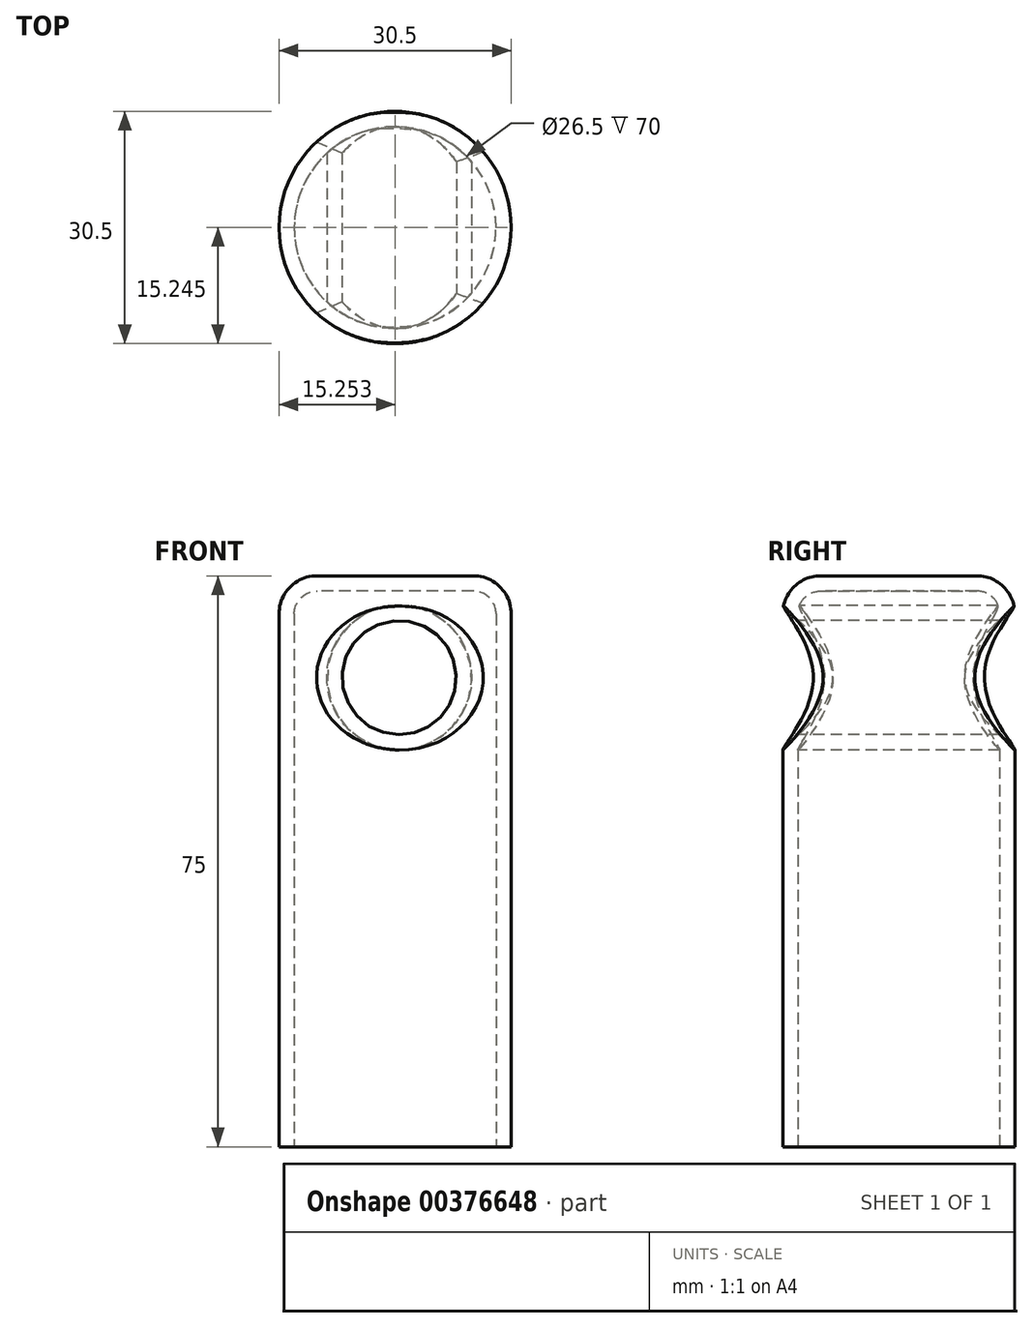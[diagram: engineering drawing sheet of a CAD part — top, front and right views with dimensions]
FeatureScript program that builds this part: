
annotation { "Feature Type Name" : "Feature", "Feature Type Description" : "" }
export const myFeature = defineFeature(function(context is Context, id is Id, definition is map)
    precondition{}
    {
        {
            var Q0;
            Q0=qCreatedBy(makeId("Top.planeOp"),FACE);
            var sketch = newSketch(context, id + "F0", { "sketchPlane" : qUnion([Q0])});
            skCircle(sketch, "E0", {"center": v(11.26, 11.54) * mm, "radius": 13.25 * mm});
            skCircle(sketch, "E1", {"center": v(11.26, 11.54) * mm, "radius": 15.25 * mm});
            skSolve(sketch);
        }
        {
            var Q0;
            Q0 = qSketchRegion(id + "F0", true);
            extrude(context, id + "F1", {"entities" : qUnion([Q0]), "depth" : 50 * mm});
        }
        {
            var Q0;
            Q0=makeQuery(id+"F1.opExtrude","CAP_FACE",FACE,{"disambiguationData":[OSD([sQuery(id+"F0.wireOp",EDGE,"E0"),sQuery(id+"F0.wireOp",EDGE,"E1")])],"isStart":false});
            var sketch = newSketch(context, id + "F2", { "sketchPlane" : qUnion([Q0])});
            skCircle(sketch, "E2", {"center": v(11.26, 11.54) * mm, "radius": 15.25 * mm});
            skSolve(sketch);
        }
        {
            var Q0;
            Q0 = qSketchRegion(id + "F2", true);
            extrude(context, id + "F3", {"entities" : qUnion([Q0]), "operationType" : NewBodyOperationType.ADD, "depth" : 25 * mm});
        }
        {
            var Q0;
            Q0=makeQuery(id+"F3.opExtrude","CAP_EDGE",EDGE,{"disambiguationData":[OSD([sQuery(id+"F2.wireOp",EDGE,"E2")])],"isStart":false});
            chamfer(context, id + "F4", {"entities" : qUnion([Q0]), "chamferType" : ChamferType.OFFSET_ANGLE, "width" : 14 * mm, "oppositeDirection" : false, "angle" : 60 * degree, "tangentPropagation" : true});
        }
        {
            var Q0;
            Q0=makeQuery(id+"F3.opExtrude","CAP_FACE",FACE,{"disambiguationData":[OSD([sQuery(id+"F2.wireOp",EDGE,"E2")])],"isStart":true});
            shell(context, id + "F5", {"entities" : qUnion([Q0]), "thickness" : 2 * mm});
        }
        {
            var Q0;
            Q0=makeQuery(id+"F3.opExtrude","CAP_FACE",FACE,{"disambiguationData":[OSD([sQuery(id+"F2.wireOp",EDGE,"E2")])],"isStart":false});
            var sketch = newSketch(context, id + "F6", { "sketchPlane" : qUnion([Q0])});
            skCircle(sketch, "E3", {"center": v(11.26, 11.54) * mm, "radius": 15.25 * mm});
            skSolve(sketch);
        }
        {
            var Q0;
            Q0 = qSketchRegion(id + "F6", true);
            extrude(context, id + "F7", {"entities" : qUnion([Q0]), "operationType" : NewBodyOperationType.ADD, "oppositeDirection" : true, "depth" : 25 * mm});
        }
        {
            var Q0;
            Q0=qCreatedBy(makeId("Front.planeOp"),FACE);
            var sketch = newSketch(context, id + "F8", { "sketchPlane" : qUnion([Q0])});
            skCircle(sketch, "E4", {"center": v(11.8, 61.62) * mm, "radius": 7.5 * mm});
            skSolve(sketch);
        }
        {
            var Q0;
            Q0 = qSketchRegion(id + "F8", true);
            extrude(context, id + "F9", {"entities" : qUnion([Q0]), "operationType" : NewBodyOperationType.REMOVE, "endBound" : BoundingType.THROUGH_ALL, "oppositeDirection" : true, "depth" : 25 * mm, "hasSecondDirection" : true, "secondDirectionBound" : SecondDirectionBoundingType.THROUGH_ALL, "secondDirectionOppositeDirection" : false, "secondDirectionDepth" : 25 * mm});
        }
        {
            var Q0;
            Q0=makeQuery(id+"F7.opExtrude","CAP_EDGE",EDGE,{"disambiguationData":[OSD([sQuery(id+"F6.wireOp",EDGE,"E3")])],"isStart":true});
            fillet(context, id + "F10", {"entities" : qUnion([Q0]), "radius" : 5 * mm, "tangentPropagation" : true, "allowEdgeOverflow" : false});
        }
        {
            var Q0;
            Q0=makeQuery(id+"F7.opExtrude","CAP_FACE",FACE,{"disambiguationData":[OSD([sQuery(id+"F6.wireOp",EDGE,"E3")])],"isStart":false});
            shell(context, id + "F11", {"entities" : qUnion([Q0]), "thickness" : 2 * mm});
        }
        {
            var Q0;
            Q0=makeQuery(id+"F9.boolean.opBoolean","INTERSECT",EDGE,{"disambiguationData":[OD(1.0)],"derivedFrom":[makeQuery(id+"F7.boolean.opBoolean","MERGE",FACE,{"derivedFrom":[makeQuery(id+"F3.boolean.opBoolean","MERGE",FACE,{"derivedFrom":[makeQuery(id+"F1.opExtrude","SWEPT_FACE",FACE,{"disambiguationData":[OSD([sQuery(id+"F0.wireOp",EDGE,"E1")])]}),makeQuery(id+"F3.opExtrude","SWEPT_FACE",FACE,{"disambiguationData":[OSD([sQuery(id+"F2.wireOp",EDGE,"E2")])]})]}),makeQuery(id+"F7.opExtrude","SWEPT_FACE",FACE,{"disambiguationData":[OSD([sQuery(id+"F6.wireOp",EDGE,"E3")])]})]}),makeQuery(id+"F9.opExtrude","SWEPT_FACE",FACE,{"disambiguationData":[OSD([sQuery(id+"F8.wireOp",EDGE,"E4")])]})]});
            var Q1;
            Q1=makeQuery(id+"F9.boolean.opBoolean","INTERSECT",EDGE,{"disambiguationData":[OD(0.0)],"derivedFrom":[makeQuery(id+"F7.boolean.opBoolean","MERGE",FACE,{"derivedFrom":[makeQuery(id+"F3.boolean.opBoolean","MERGE",FACE,{"derivedFrom":[makeQuery(id+"F1.opExtrude","SWEPT_FACE",FACE,{"disambiguationData":[OSD([sQuery(id+"F0.wireOp",EDGE,"E1")])]}),makeQuery(id+"F3.opExtrude","SWEPT_FACE",FACE,{"disambiguationData":[OSD([sQuery(id+"F2.wireOp",EDGE,"E2")])]})]}),makeQuery(id+"F7.opExtrude","SWEPT_FACE",FACE,{"disambiguationData":[OSD([sQuery(id+"F6.wireOp",EDGE,"E3")])]})]}),makeQuery(id+"F9.opExtrude","SWEPT_FACE",FACE,{"disambiguationData":[OSD([sQuery(id+"F8.wireOp",EDGE,"E4")])]})]});
            chamfer(context, id + "F12", {"entities" : qUnion([Q0, Q1]), "width" : 2 * mm, "tangentPropagation" : true});
        }
    });
